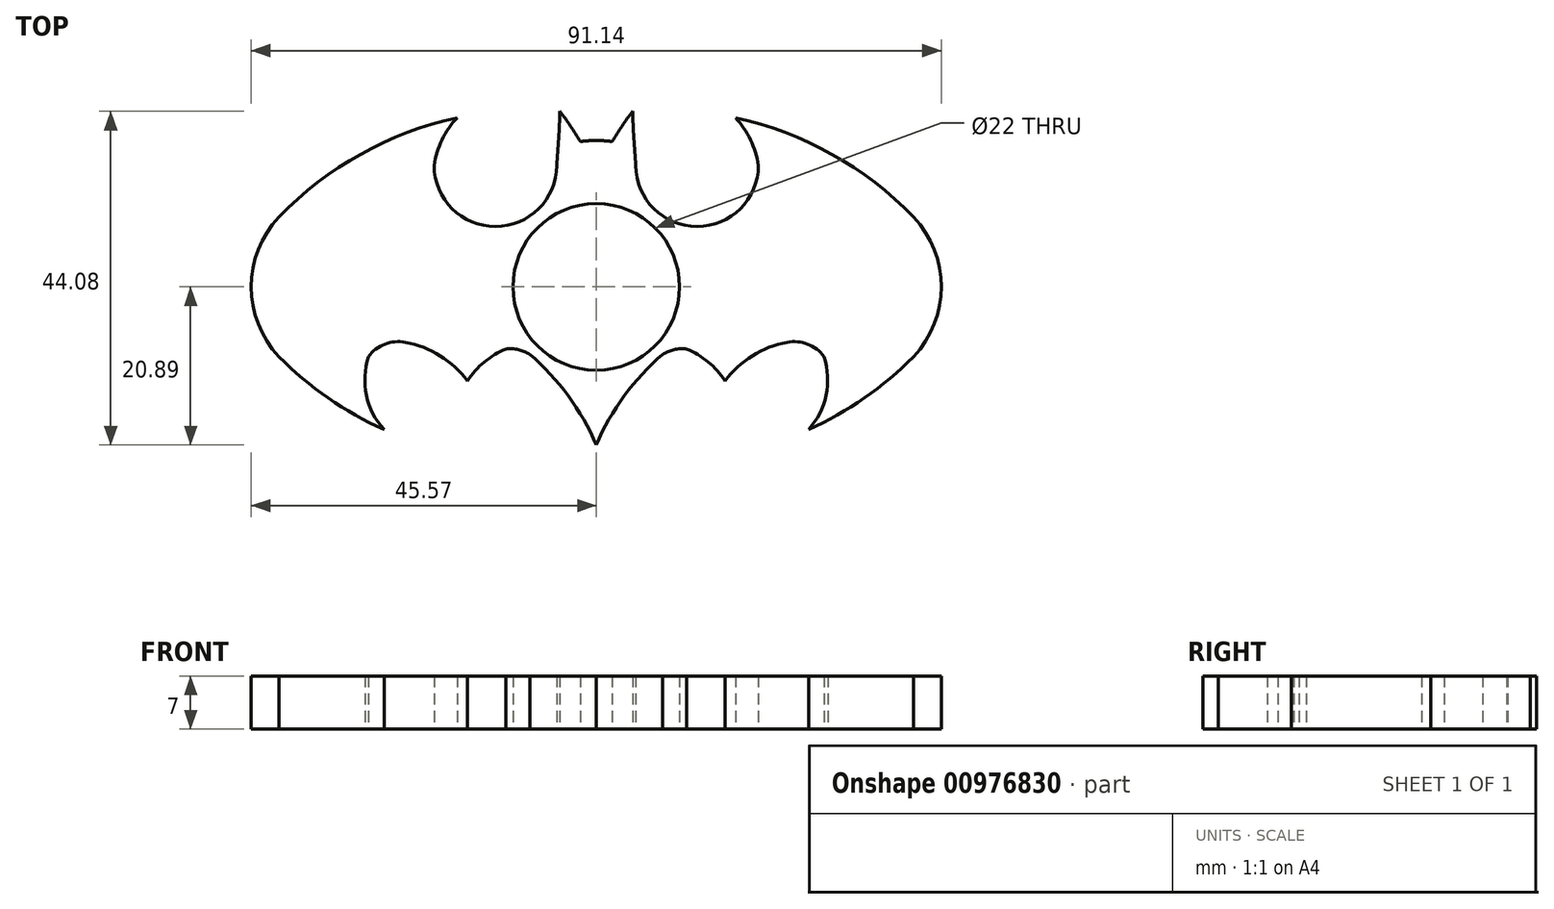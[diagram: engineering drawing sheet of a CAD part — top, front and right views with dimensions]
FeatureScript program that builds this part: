
annotation { "Feature Type Name" : "Feature", "Feature Type Description" : "" }
export const myFeature = defineFeature(function(context is Context, id is Id, definition is map)
    precondition{}
    {
        {
            var Q0;
            Q0=qCreatedBy(makeId("Top.planeOp"),FACE);
            var sketch = newSketch(context, id + "F0", { "sketchPlane" : qUnion([Q0])});
            skLineSegment(sketch, "E0", {"start": v(0, 90) * mm, "end": v(0, -90) * mm, "construction": true});
            skCircle(sketch, "E1", {"center": v(0, 0) * mm, "radius": 11 * mm});
            skArc(sketch, "E2", {"start": v(2.11, 19.2) * mm, "mid": v(1.06, 19.3) * mm, "end": v(0, 19.34) * mm});
            skArc(sketch, "E3", {"start": v(4.8, 23.19) * mm, "mid": v(3.4, 21.24) * mm, "end": v(2.11, 19.2) * mm});
            skArc(sketch, "E4", {"start": v(5.23, 16.04) * mm, "mid": v(13.32, 7.96) * mm, "end": v(21.4, 16.04) * mm});
            skArc(sketch, "E5", {"start": v(21.4, 16.04) * mm, "mid": v(20.38, 19.41) * mm, "end": v(18.38, 22.32) * mm});
            skArc(sketch, "E6", {"start": v(41.93, 9.23) * mm, "mid": v(31.12, 17.5) * mm, "end": v(18.38, 22.32) * mm});
            skArc(sketch, "E7", {"start": v(4.8, 23.19) * mm, "mid": v(4.96, 19.61) * mm, "end": v(5.23, 16.04) * mm});
            skArc(sketch, "E8", {"start": v(41.93, -9.23) * mm, "mid": v(45.57, 0) * mm, "end": v(41.93, 9.23) * mm});
            skArc(sketch, "E9", {"start": v(28.04, -18.86) * mm, "mid": v(35.41, -14.67) * mm, "end": v(41.93, -9.23) * mm});
            skArc(sketch, "E10", {"start": v(28.04, -18.86) * mm, "mid": v(30.36, -14.32) * mm, "end": v(30.1, -9.23) * mm});
            skArc(sketch, "E11", {"start": v(30.1, -9.23) * mm, "mid": v(27.92, -7.57) * mm, "end": v(25.2, -7.32) * mm});
            skArc(sketch, "E12", {"start": v(25.2, -7.32) * mm, "mid": v(20.63, -9.1) * mm, "end": v(17, -12.4) * mm});
            skArc(sketch, "E13", {"start": v(17, -12.4) * mm, "mid": v(14.78, -9.92) * mm, "end": v(11.93, -8.2) * mm});
            skArc(sketch, "E14", {"start": v(11.93, -8.2) * mm, "mid": v(10.3, -8.3) * mm, "end": v(8.77, -8.9) * mm});
            skArc(sketch, "E15", {"start": v(8.77, -8.9) * mm, "mid": v(3.7, -14.4) * mm, "end": v(0, -20.89) * mm});
            skArc(sketch, "E16.MirrorCS", {"start": v(-11.93, -8.2) * mm, "mid": v(-10.3, -8.3) * mm, "end": v(-8.77, -8.9) * mm});
            skArc(sketch, "E17.MirrorCS", {"start": v(-2.11, 19.2) * mm, "mid": v(-1.06, 19.3) * mm, "end": v(0, 19.34) * mm});
            skArc(sketch, "E18.MirrorCS", {"start": v(-17, -12.4) * mm, "mid": v(-14.78, -9.92) * mm, "end": v(-11.93, -8.2) * mm});
            skArc(sketch, "E19.MirrorCS", {"start": v(-4.8, 23.19) * mm, "mid": v(-3.4, 21.24) * mm, "end": v(-2.11, 19.2) * mm});
            skArc(sketch, "E20.MirrorCS", {"start": v(-25.2, -7.32) * mm, "mid": v(-20.63, -9.1) * mm, "end": v(-17, -12.4) * mm});
            skArc(sketch, "E21.MirrorCS", {"start": v(-4.8, 23.19) * mm, "mid": v(-4.96, 19.61) * mm, "end": v(-5.23, 16.04) * mm});
            skArc(sketch, "E22.MirrorCS", {"start": v(-41.93, 9.23) * mm, "mid": v(-31.12, 17.5) * mm, "end": v(-18.38, 22.32) * mm});
            skArc(sketch, "E23.MirrorCS", {"start": v(-41.93, -9.23) * mm, "mid": v(-45.57, 0) * mm, "end": v(-41.93, 9.23) * mm});
            skArc(sketch, "E24.MirrorCS", {"start": v(-21.4, 16.04) * mm, "mid": v(-20.38, 19.41) * mm, "end": v(-18.38, 22.32) * mm});
            skArc(sketch, "E25.MirrorCS", {"start": v(-28.04, -18.86) * mm, "mid": v(-30.36, -14.32) * mm, "end": v(-30.1, -9.23) * mm});
            skArc(sketch, "E26.MirrorCS", {"start": v(-30.1, -9.23) * mm, "mid": v(-27.92, -7.57) * mm, "end": v(-25.2, -7.32) * mm});
            skArc(sketch, "E27.MirrorCS", {"start": v(-8.77, -8.9) * mm, "mid": v(-3.7, -14.4) * mm, "end": v(0, -20.89) * mm});
            skArc(sketch, "E28.MirrorCS", {"start": v(-28.04, -18.86) * mm, "mid": v(-35.41, -14.67) * mm, "end": v(-41.93, -9.23) * mm});
            skArc(sketch, "E29.MirrorCS", {"start": v(-5.23, 16.04) * mm, "mid": v(-13.32, 7.96) * mm, "end": v(-21.4, 16.04) * mm});
            skSolve(sketch);
        }
        {
            var Q0;
            Q0=makeQuery(id+"F0.imprint","IMPRINT",FACE,{"disambiguationData":[TD([[makeQuery(id+"F0.imprint","IMPRINT",EDGE,{"derivedFrom":sQuery(id+"F0.wireOp",EDGE,"E1")}),-1.0]])]});
            extrude(context, id + "F1", {"entities" : qUnion([Q0]), "depth" : 7 * mm, "offsetDistance" : 25 * mm, "symmetric" : true});
        }
    });
